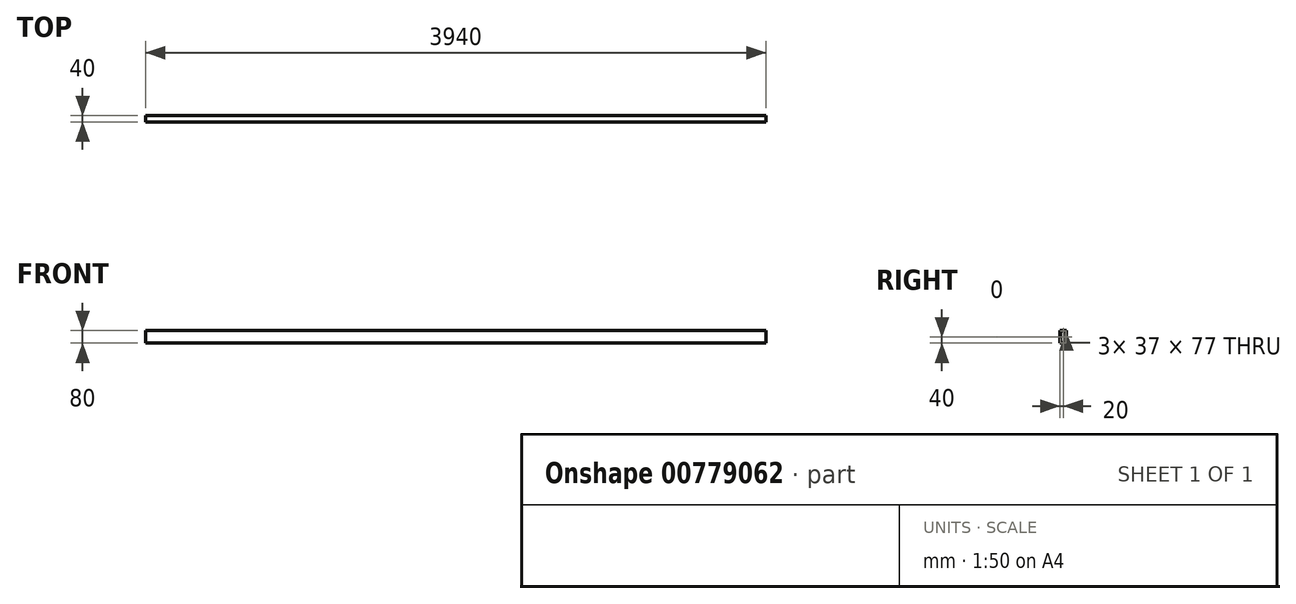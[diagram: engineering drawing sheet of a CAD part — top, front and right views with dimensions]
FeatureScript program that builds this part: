
annotation { "Feature Type Name" : "Feature", "Feature Type Description" : "" }
export const myFeature = defineFeature(function(context is Context, id is Id, definition is map)
    precondition{}
    {
        {
            var Q0;
            Q0=qCreatedBy(makeId("Right.planeOp"),FACE);
            var sketch = newSketch(context, id + "F0", { "sketchPlane" : qUnion([Q0])});
            skLineSegment(sketch, "E0.bottom", {"start": v(20, 40) * mm, "end": v(-20, 40) * mm});
            skLineSegment(sketch, "E0.top", {"start": v(20, -40) * mm, "end": v(-20, -40) * mm});
            skLineSegment(sketch, "E0.left", {"start": v(20, 40) * mm, "end": v(20, -40) * mm});
            skLineSegment(sketch, "E0.right", {"start": v(-20, 40) * mm, "end": v(-20, -40) * mm});
            skPoint(sketch, "E0.middle", {"position": v(0, 0) * mm});
            skLineSegment(sketch, "E1.bottom", {"start": v(18.5, 38.5) * mm, "end": v(-18.5, 38.5) * mm});
            skLineSegment(sketch, "E1.top", {"start": v(18.5, -38.5) * mm, "end": v(-18.5, -38.5) * mm});
            skLineSegment(sketch, "E1.left", {"start": v(18.5, 38.5) * mm, "end": v(18.5, -38.5) * mm});
            skLineSegment(sketch, "E1.right", {"start": v(-18.5, 38.5) * mm, "end": v(-18.5, -38.5) * mm});
            skSolve(sketch);
        }
        {
            var Q0;
            Q0=makeQuery(id+"F0.imprint","IMPRINT",FACE,{"disambiguationData":[TD([[makeQuery(id+"F0.imprint","IMPRINT",EDGE,{"derivedFrom":sQuery(id+"F0.wireOp",EDGE,"E0.bottom")}),1.0]])]});
            extrude(context, id + "F1", {"entities" : qUnion([Q0]), "depth" : 3940 * mm, "offsetDistance" : 25 * mm});
        }
    });
